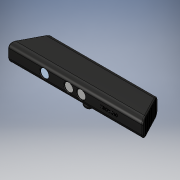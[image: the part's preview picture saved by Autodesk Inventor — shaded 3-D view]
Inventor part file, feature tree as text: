
AUTODESK INVENTOR PART (.ipt)
format: ipt  version: 2018 (Build 220112000, 112)  size: 574,976 bytes
history: native  units: in
note: dims shown in document units (in); Inventor stores cm internally (conversion verified against a paired STEP export)
features: fillet x1
ambient origin geometry x8: Origin, YZ Plane, XZ Plane, XY Plane, X Axis, Y Axis, Z Axis, Center Point
bodies: Solid1 (feature_tree)
feature tree (1):
  fillet  "Fillet3"  [1 undecoded]
note: 1 required parameter value undecoded (feature->parameter linkage not recoverable at this tier; creation-order binding heuristic only, values carry confidence <= 0.55)
